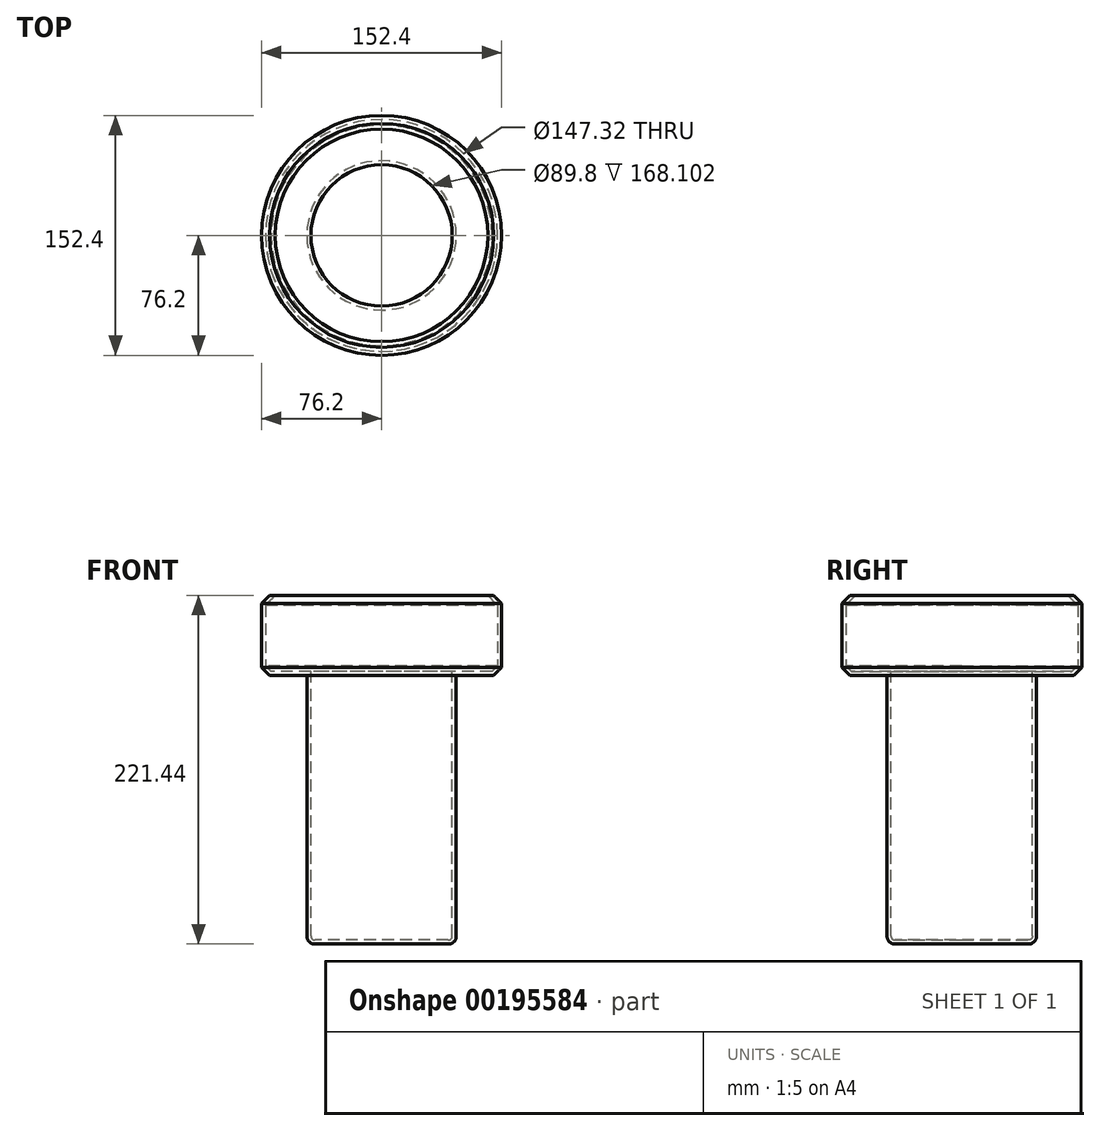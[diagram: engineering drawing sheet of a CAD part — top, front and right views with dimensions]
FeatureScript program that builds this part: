
annotation { "Feature Type Name" : "Feature", "Feature Type Description" : "" }
export const myFeature = defineFeature(function(context is Context, id is Id, definition is map)
    precondition{}
    {
        {
            var Q0;
            Q0=qCreatedBy(makeId("Top.planeOp"),FACE);
            var sketch = newSketch(context, id + "F0", { "sketchPlane" : qUnion([Q0])});
            skCircle(sketch, "E0", {"center": v(0, 0) * mm, "radius": 76.2 * mm});
            skSolve(sketch);
        }
        {
            var Q0;
            Q0=makeQuery(id+"F0.imprint","IMPRINT",FACE,{"disambiguationData":[TD([[makeQuery(id+"F0.imprint","IMPRINT",EDGE,{"derivedFrom":sQuery(id+"F0.wireOp",EDGE,"E0")}),1.0]])]});
            extrude(context, id + "F1", {"entities" : qUnion([Q0]), "depth" : 50.8 * mm});
        }
        {
            var Q0;
            Q0=makeQuery(id+"F1.opExtrude","CAP_FACE",FACE,{"disambiguationData":[OSD([sQuery(id+"F0.wireOp",EDGE,"E0")])],"isStart":false});
            var sketch = newSketch(context, id + "F2", { "sketchPlane" : qUnion([Q0])});
            skCircle(sketch, "E1", {"center": v(0, 0) * mm, "radius": 47.44 * mm});
            skSolve(sketch);
        }
        {
            var Q0;
            Q0=makeQuery(id+"F2.imprint","IMPRINT",FACE,{"disambiguationData":[TD([[makeQuery(id+"F2.imprint","IMPRINT",EDGE,{"derivedFrom":sQuery(id+"F2.wireOp",EDGE,"E1")}),1.0]])]});
            extrude(context, id + "F3", {"entities" : qUnion([Q0]), "operationType" : NewBodyOperationType.ADD, "endBound" : BoundingType.THROUGH_ALL, "oppositeDirection" : true, "depth" : 25.4 * mm});
        }
        {
            var Q0;
            Q0=makeQuery(id+"F1.opExtrude","CAP_EDGE",EDGE,{"disambiguationData":[OSD([sQuery(id+"F0.wireOp",EDGE,"E0")])],"isStart":false});
            var Q1;
            Q1=makeQuery(id+"F1.opExtrude","CAP_EDGE",EDGE,{"disambiguationData":[OSD([sQuery(id+"F0.wireOp",EDGE,"E0")])],"isStart":true});
            chamfer(context, id + "F4", {"entities" : qUnion([Q0, Q1]), "width" : 5.08 * mm, "tangentPropagation" : true});
        }
        {
            var Q0;
            Q0=makeQuery(id+"F3.opExtrude","CAP_EDGE",EDGE,{"disambiguationData":[OSD([sQuery(id+"F2.wireOp",EDGE,"E1")])],"isStart":false});
            fillet(context, id + "F5", {"entities" : qUnion([Q0]), "radius" : 5.08 * mm, "tangentPropagation" : true, "allowEdgeOverflow" : false});
        }
        {
            var Q0;
            Q0=makeQuery(id+"F1.opExtrude","CAP_FACE",FACE,{"disambiguationData":[OSD([sQuery(id+"F0.wireOp",EDGE,"E0")])],"isStart":false});
            shell(context, id + "F6", {"entities" : qUnion([Q0]), "thickness" : 2.54 * mm});
        }
    });
